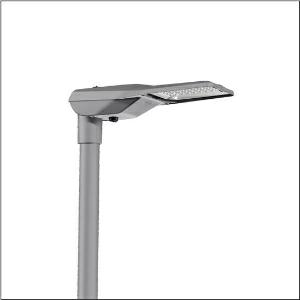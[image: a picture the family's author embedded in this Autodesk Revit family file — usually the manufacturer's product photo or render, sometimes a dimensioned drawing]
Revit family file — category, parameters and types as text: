
# Revit family: streetlight_sl_21_iq_mini___st1_0a_5xe2d41y08hb_48d2
name_source: partatom
category: Lighting Fixtures
units: mm (PartAtom-declared; Revit-internal decimal feet)

## family parameters
Cut with Voids When Loaded = No
Host = Face
Light Source = No
Part Type = Normal
Room Calculation Point = No
Round Connector Dimension = Use Diameter
Shared = No

## types (1)
- --- (1 x LED, 10080 lm, 71 W, 4000K)
    Apparent Load = 71 VA
    CIE Flux Codes = 37 72 97 100 100
    Color Rendering = 70
    Color Temperature = 4000K
    Default Elevation = 1800 mm
    Description = Streetlight SL 21 iQ mini, mast luminaire, primary light control with lens, of PMMA, primary optical cover: cover, of toughened safety glass, transparent, light distribution: ST1.0a, light emission: direct distribution, primary light characteristic: asymmetric, installation type: post-top, side-entry, LED, High Power LED, rated luminous flux: 10.080lm, luminous efficacy: 142lm/W, light colour: 740, colour temperature: 4000K, control: presetting dimming logarithmic, Street-Remote, Auto-Match, Temp-Guard, Lumen-Switch, Night-Set, Smart-Wire, Light-Fading, Desk-Remote (wireless, voltage-free reading and setting of iQ features in the workshop via application-optimized NFC function/RFID function), optimised constant luminous flux control (CLO 2.0), mains connection: 220..240V, AC, 50/60Hz, start of lifetime: 71W, end of service life: 75W, reduction: 31W, luminaire housing, of diecast aluminium, powder-coated, Siteco® metallic grey (DB 702S), corrosivity category C5 mid according to DIN EN ISO 12944, please order mast flange separately, inclination adjustable: 0°, 5°, 10°, 15°, sealing non-destructively replaceable, multi-level sealing system, length: 628mm, width: 235mm, height: 110mm, mast flange for spigot size: 42mm (side-entry): 5XC10008XM4, 60/48mm (side-entry/post-top): 5XC10108XM2, 76/60mm (side-entry/post-top): 5XC10108XM1, Smart Interface below and above, protection rating (complete): IP66, insulation class (complete): insulation class II (safety insulation), certification: CE, ENEC, ENEC+, VDE, impact resistance: IK09, permissible operating ambient temperature for outdoor applications: -40..+50°C, standard-compliant lighting for roads and squares, packaging unit: 1 piece

Light Distribution: ST1.0a
    Height = 110 mm
    Lamp = 1 x LED
    Lamp Light Flux = 10080 lm
    Lamp Power = 71 W
    Lamp count = 1
    Length = 625 mm
    Luminous efficacy = 142 lm/W
    Manufacturer = Siteco
    ModVariant = No
    Model = 5XE2D41Y08HB
    Number of Poles = 1
    OnlyDefault = Yes
    Power Factor = 1
    Product Name = Streetlight SL 21 iQ mini | ST1.0a
    Product group = mast luminaire | pylon top
    ProductGroupID = 6100
    Protection Class = Protection class II
    Protection Degree = IP 66
    RLX_Detail_Level = 1
    RLX_Emergency_Light_Flux = 0 lm
    RLX_Emergency_Type = 0
    RLX_Emergency_Type_DB = No
    RlxData = <blob elided: 92769 chars, md5=e8b61473>
    Socket = socket
    Standby Power = 0 W
    System Light Flux = 10080 lm
    System Power = 71 W
    Type Comments = factory setting: luminous flux: 100 % | dim-lin: 254 | 716 mA
    Type Image = l_1003514.jpg
    URL = http://relux.com
    VarID = @adj_044759
    Voltage = 0 V
    Weight = 0.00 kg
    Width = 234 mm

## geometry (parser evidence)
native form markers: Blend x4, Sweep x12
no freeform markers — native parametric forms only
